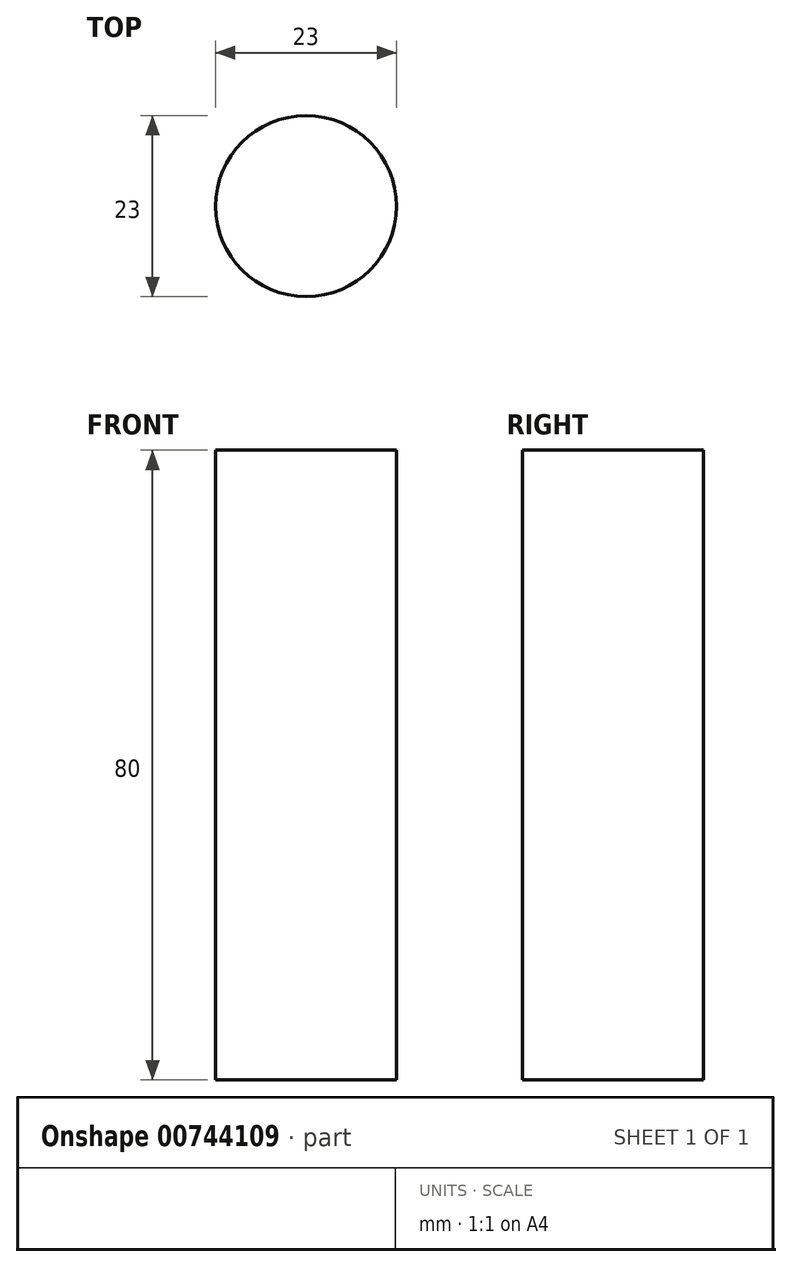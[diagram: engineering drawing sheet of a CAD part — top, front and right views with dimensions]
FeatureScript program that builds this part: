
annotation { "Feature Type Name" : "Feature", "Feature Type Description" : "" }
export const myFeature = defineFeature(function(context is Context, id is Id, definition is map)
    precondition{}
    {
        {
            var Q0;
            Q0=qCreatedBy(makeId("Top.planeOp"),FACE);
            var sketch = newSketch(context, id + "F0", { "sketchPlane" : qUnion([Q0])});
            skCircle(sketch, "E0", {"center": v(0, 0) * mm, "radius": 11.5 * mm});
            skSolve(sketch);
        }
        {
            var Q0;
            Q0=makeQuery(id+"F0.imprint","IMPRINT",FACE,{"disambiguationData":[TD([[makeQuery(id+"F0.imprint","IMPRINT",EDGE,{"derivedFrom":sQuery(id+"F0.wireOp",EDGE,"E0")}),1.0]])]});
            extrude(context, id + "F1", {"entities" : qUnion([Q0]), "depth" : 80 * mm, "offsetDistance" : 25 * mm});
        }
    });
